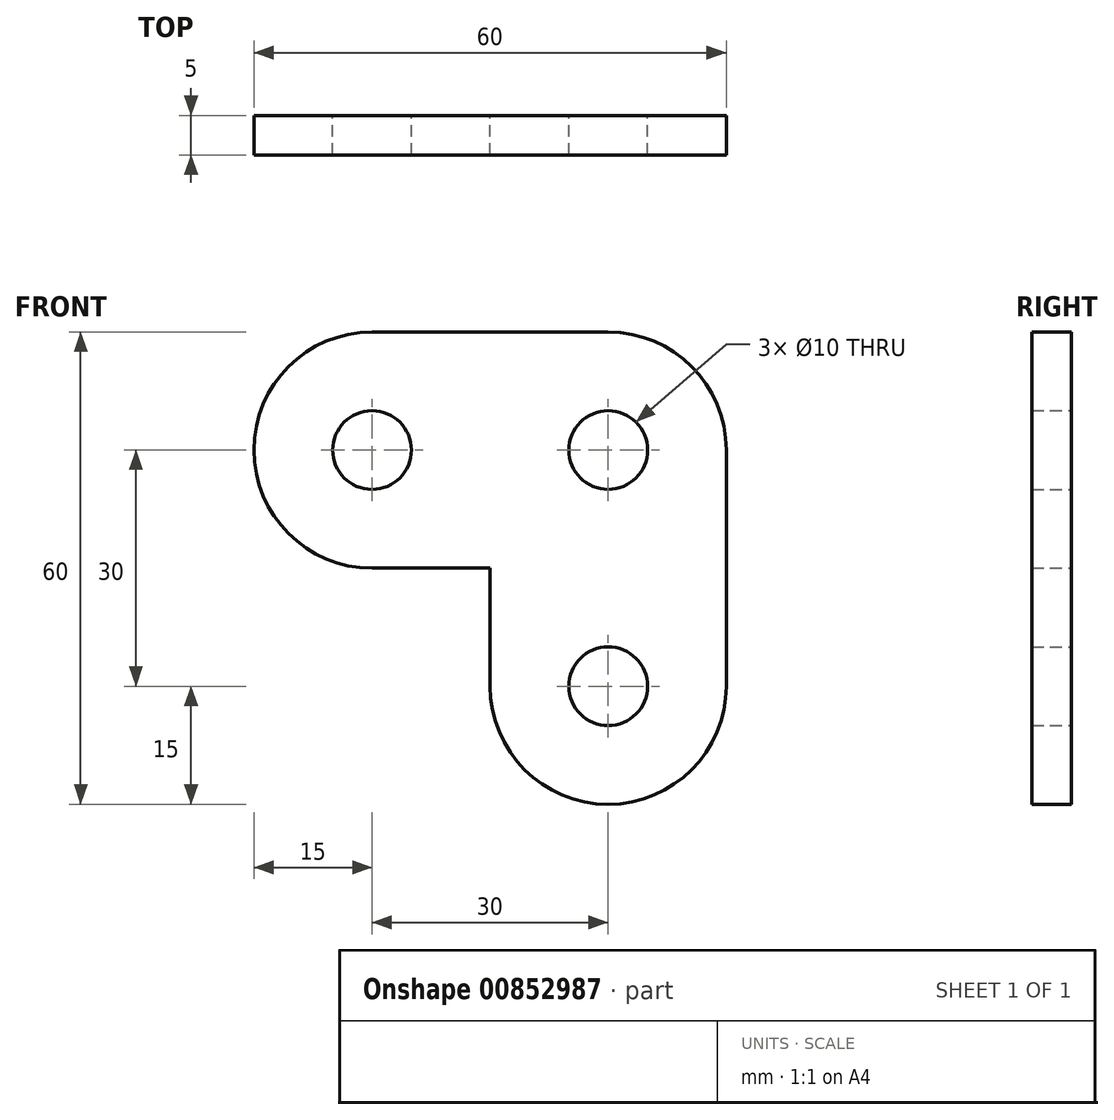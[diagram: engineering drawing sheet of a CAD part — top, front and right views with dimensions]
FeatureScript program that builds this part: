
annotation { "Feature Type Name" : "Feature", "Feature Type Description" : "" }
export const myFeature = defineFeature(function(context is Context, id is Id, definition is map)
    precondition{}
    {
        {
            var Q0;
            Q0=qCreatedBy(makeId("Front.planeOp"),FACE);
            var sketch = newSketch(context, id + "F0", { "sketchPlane" : qUnion([Q0])});
            skLineSegment(sketch, "E0.bottom", {"start": v(15, 0) * mm, "end": v(45, 0) * mm});
            skLineSegment(sketch, "E0.right", {"start": v(60, -15) * mm, "end": v(60, -45) * mm});
            skCircle(sketch, "E1", {"center": v(45, -15) * mm, "radius": 5 * mm});
            skCircle(sketch, "E2", {"center": v(15, -15) * mm, "radius": 5 * mm});
            skCircle(sketch, "E3", {"center": v(45, -45) * mm, "radius": 5 * mm});
            skLineSegment(sketch, "E4.top", {"start": v(15, -30) * mm, "end": v(30, -30) * mm});
            skLineSegment(sketch, "E4.right", {"start": v(30, -45) * mm, "end": v(30, -30) * mm});
            skArc(sketch, "E5", {"start": v(15, 0) * mm, "mid": v(0, -15) * mm, "end": v(15, -30) * mm});
            skArc(sketch, "E6", {"start": v(30, -45) * mm, "mid": v(45, -60) * mm, "end": v(60, -45) * mm});
            skArc(sketch, "E7", {"start": v(60, -15) * mm, "mid": v(55.6, -4.4) * mm, "end": v(45, 0) * mm});
            skSolve(sketch);
        }
        {
            var Q0;
            Q0=makeQuery(id+"F0.imprint","IMPRINT",FACE,{"disambiguationData":[TD([[makeQuery(id+"F0.imprint","IMPRINT",EDGE,{"derivedFrom":sQuery(id+"F0.wireOp",EDGE,"E0.bottom")}),-1.0]])]});
            extrude(context, id + "F1", {"entities" : qUnion([Q0]), "depth" : 5 * mm, "offsetDistance" : 25 * mm});
        }
    });
